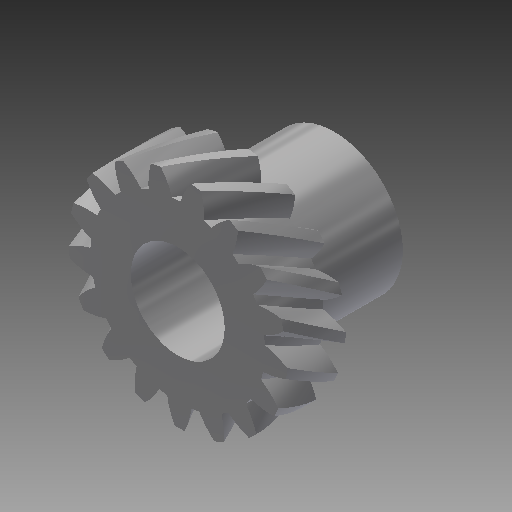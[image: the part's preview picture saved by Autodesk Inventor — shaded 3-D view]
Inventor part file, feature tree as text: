
AUTODESK INVENTOR PART (.ipt)
format: ipt  version: 2018 (Build 220112000, 112)  size: 526,848 bytes
history: native  units: mm (DEFAULTED — no unit token found)
features: sketch x5, extrude x4, plane x3, other x3, projected_geometry x1
ambient origin geometry x8: Origin, YZ Plane, XZ Plane, XY Plane, X Axis, Y Axis, Z Axis, Center Point
bodies: Solid1 (feature_tree)
feature tree (16):
  extrude  "Extrusion1"  Depth=10.16mm TaperAngle=0.0deg
  plane  "Work Plane1"
  plane  "Work Plane2"
  plane  "Work Plane3"
  other  "Spur Gear"
  extrude  "Extrusion2"  Depth=76.2mm TaperAngle=0.0deg
  extrude  "Extrusion3"  TaperAngle=0.0deg  [1 undecoded]
  extrude  "Extrusion4"  Depth=31.75mm
  sketch  "Sketch1"  dims[d0=14.176796mm d1=10.16mm d2=0.0mm]
  sketch  "Sketch2"  dims[d3=12.552326mm d4=76.2mm d5=0.0mm]
  other  "Srf1"
  sketch  "Sketch3"  dims[d6=0.0mm d7=1.847996mm d9=0.0mm]
  sketch  "Sketch4"  dims[d14=0.0mm d15=31.75mm]
  projected_geometry  "Projected Loop1"
  sketch  "Sketch5"  dims[d16=0.0mm d17=0.0mm d18=0.0mm d19=31.75mm d20=6.096mm d21=25.4mm d22=0.0mm d23=8.89mm d24=6.35mm d25=0.0mm d26=2.54mm d27=6.35mm d28=0.0mm]
  other  "Pitch Diameter"
note: 1 required parameter value undecoded (feature->parameter linkage not recoverable at this tier; creation-order binding heuristic only, values carry confidence <= 0.55)
